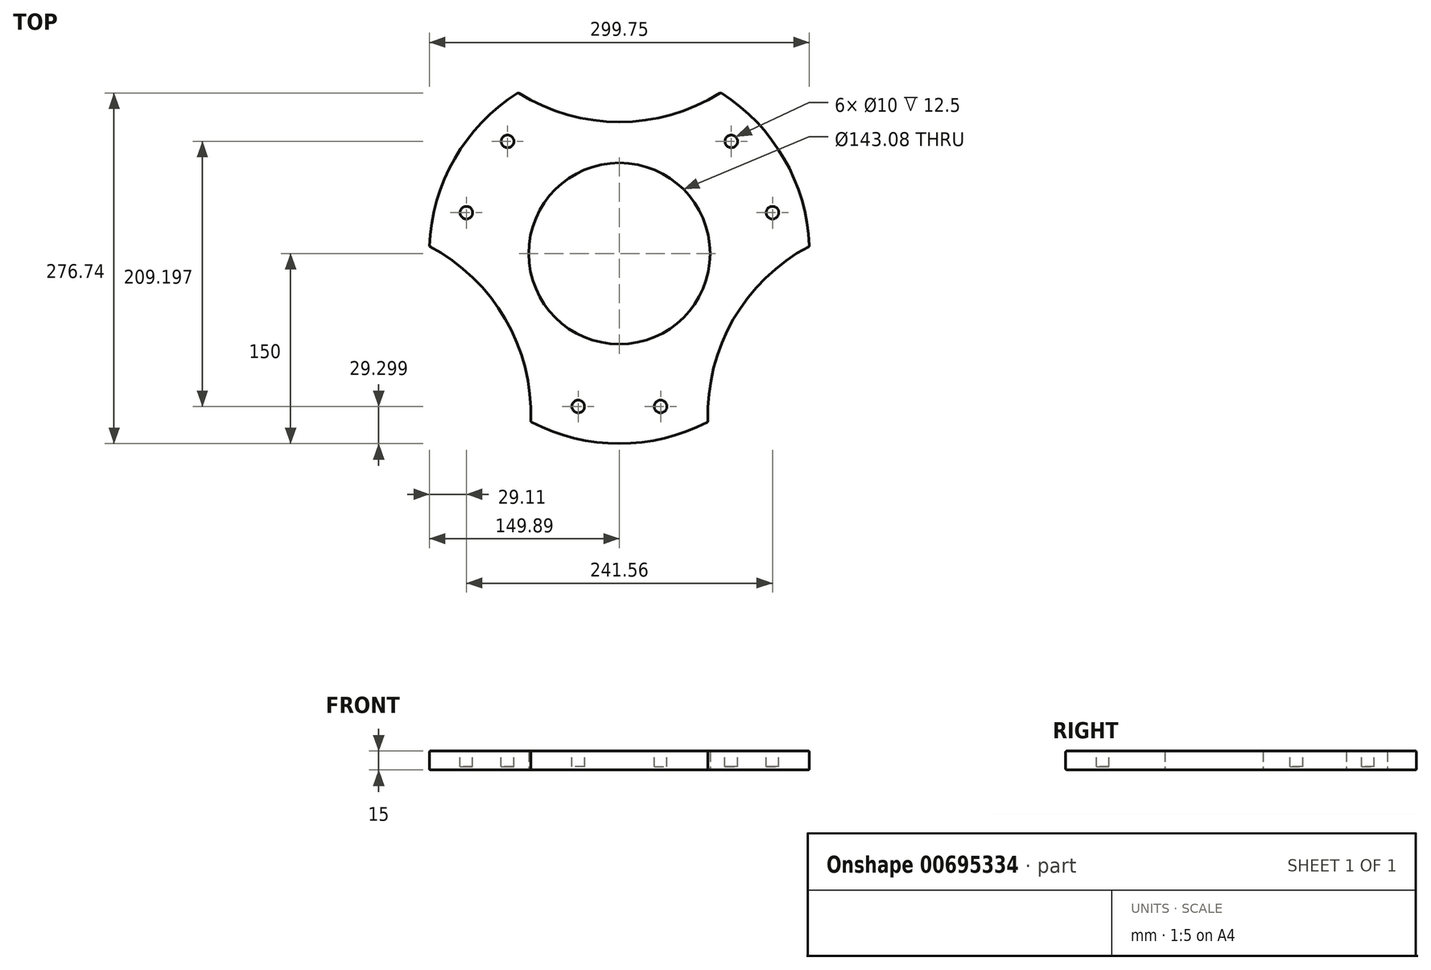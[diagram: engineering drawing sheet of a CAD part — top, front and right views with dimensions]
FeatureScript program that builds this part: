
annotation { "Feature Type Name" : "Feature", "Feature Type Description" : "" }
export const myFeature = defineFeature(function(context is Context, id is Id, definition is map)
    precondition{}
    {
        {
            var Q0;
            Q0=qCreatedBy(makeId("Top.planeOp"),FACE);
            var sketch = newSketch(context, id + "F0", { "sketchPlane" : qUnion([Q0])});
            skLineSegment(sketch, "E0", {"start": v(0, 0) * mm, "end": v(0, -150) * mm, "construction": true});
            skArc(sketch, "E1", {"start": v(-61.95, 35.77) * mm, "mid": v(-61.95, -35.77) * mm, "end": v(0, -71.54) * mm});
            skArc(sketch, "E2", {"start": v(-129.9, 75) * mm, "mid": v(-144.12, 41.6) * mm, "end": v(-149.89, 5.76) * mm});
            skLineSegment(sketch, "E3", {"start": v(0, 0) * mm, "end": v(-129.9, -75) * mm, "construction": true});
            skArc(sketch, "E4", {"start": v(-69.95, -132.69) * mm, "mid": v(-89.94, -51.93) * mm, "end": v(-149.89, 5.76) * mm});
            skLineSegment(sketch, "E5", {"start": v(0, 0) * mm, "end": v(-129.9, 75) * mm, "construction": true});
            skLineSegment(sketch, "E6", {"start": v(-129.9, 75) * mm, "end": v(-61.95, 35.77) * mm});
            skLineSegment(sketch, "E7", {"start": v(0, -71.54) * mm, "end": v(0, -150) * mm});
            skArc(sketch, "E8.trimOffspring", {"start": v(-69.95, -132.69) * mm, "mid": v(-36.03, -145.6) * mm, "end": v(0, -150) * mm});
            skSolve(sketch);
        }
        {
            var Q0;
            Q0=makeQuery(id+"F0.imprint","IMPRINT",FACE,{"disambiguationData":[TD([[makeQuery(id+"F0.imprint","IMPRINT",EDGE,{"derivedFrom":sQuery(id+"F0.wireOp",EDGE,"E1")}),-1.0]])]});
            extrude(context, id + "F1", {"entities" : qUnion([Q0]), "depth" : 15 * mm});
        }
        {
            var Q0;
            Q0=makeQuery(id+"F1.opExtrude","CAP_FACE",FACE,{"disambiguationData":[OSD([sQuery(id+"F0.wireOp",EDGE,"E1"),sQuery(id+"F0.wireOp",EDGE,"E2"),sQuery(id+"F0.wireOp",EDGE,"E4"),sQuery(id+"F0.wireOp",EDGE,"E6"),sQuery(id+"F0.wireOp",EDGE,"E7"),sQuery(id+"F0.wireOp",EDGE,"E8.trimOffspring")])],"isStart":false});
            var sketch = newSketch(context, id + "F2", { "sketchPlane" : qUnion([Q0])});
            skCircle(sketch, "E9", {"center": v(-32.5, -120.7) * mm, "radius": 5 * mm});
            skCircle(sketch, "E10", {"center": v(0, 0) * mm, "radius": 125 * mm, "construction": true});
            skLineSegment(sketch, "E11.0", {"start": v(0, 0) * mm, "end": v(-129.9, -75) * mm, "construction": true});
            skLineSegment(sketch, "E12.0", {"start": v(0, 0) * mm, "end": v(0, -150) * mm, "construction": true});
            skSolve(sketch);
        }
        {
            var Q0;
            Q0=makeQuery(id+"F2.imprint","IMPRINT",FACE,{"disambiguationData":[TD([[makeQuery(id+"F2.imprint","IMPRINT",EDGE,{"derivedFrom":sQuery(id+"F2.wireOp",EDGE,"E9")}),1.0]])]});
            extrude(context, id + "F3", {"entities" : qUnion([Q0]), "oppositeDirection" : true, "depth" : 12.5 * mm});
        }
        {
            var Q0;
            Q0=sQuery(id+"F0.wireOp",EDGE,"E3");
            cPlane(context, id + "F4", {"entities" : qUnion([Q0]), "cplaneType" : CPlaneType.LINE_ANGLE, "offset" : 150 * mm, "angle" : 0 * degree, "width" : 150 * mm, "height" : 150 * mm});
        }
        {
            var Q0;
            Q0=makeQuery(id+"F3.opExtrude","SWEPT_BODY",BODY,{"disambiguationData":[OSD([sQuery(id+"F2.wireOp",EDGE,"E9")])]});
            var Q1;
            Q1=qCreatedBy(id+"F4.planeOp",FACE);
            mirror(context, id + "F5", {"entities" : qUnion([Q0]), "mirrorPlane" : qUnion([Q1])});
        }
        {
            var Q0;
            Q0=makeQuery(id+"F3.opExtrude","SWEPT_BODY",BODY,{"disambiguationData":[OSD([sQuery(id+"F2.wireOp",EDGE,"E9")])]});
            var Q1;
            Q1=makeQuery(id+"F5.opPattern","COPY",BODY,{"derivedFrom":makeQuery(id+"F3.opExtrude","SWEPT_BODY",BODY,{"disambiguationData":[OSD([sQuery(id+"F2.wireOp",EDGE,"E9")])]}),"instanceName":"1"});
            var Q2;
            Q2=makeQuery(id+"F1.opExtrude","SWEPT_BODY",BODY,{"disambiguationData":[OSD([sQuery(id+"F0.wireOp",EDGE,"E1"),sQuery(id+"F0.wireOp",EDGE,"E2"),sQuery(id+"F0.wireOp",EDGE,"E4"),sQuery(id+"F0.wireOp",EDGE,"E6"),sQuery(id+"F0.wireOp",EDGE,"E7"),sQuery(id+"F0.wireOp",EDGE,"E8.trimOffspring")])]});
            booleanBodies(context, id + "F6", {"operationType" : BooleanOperationType.SUBTRACTION, "tools" : qUnion([Q0, Q1]), "targets" : qUnion([Q2])});
        }
        {
            var Q0;
            Q0=makeQuery(id+"F1.opExtrude","SWEPT_BODY",BODY,{"disambiguationData":[OSD([sQuery(id+"F0.wireOp",EDGE,"E1"),sQuery(id+"F0.wireOp",EDGE,"E2"),sQuery(id+"F0.wireOp",EDGE,"E4"),sQuery(id+"F0.wireOp",EDGE,"E6"),sQuery(id+"F0.wireOp",EDGE,"E7"),sQuery(id+"F0.wireOp",EDGE,"E8.trimOffspring")])]});
            var Q1;
            Q1=makeQuery(id+"F1.opExtrude","SWEPT_FACE",FACE,{"disambiguationData":[OSD([sQuery(id+"F0.wireOp",EDGE,"E1")])]});
            circularPattern(context, id + "F7", {"entities" : qUnion([Q0]), "axis" : qUnion([Q1]), "angle" : 360 * degree, "instanceCount" : 3, "equalSpace" : true, "computeTransformsWithoutBuiltin" : true});
        }
        {
            var Q0;
            Q0=makeQuery(id+"F1.opExtrude","SWEPT_BODY",BODY,{"disambiguationData":[OSD([sQuery(id+"F0.wireOp",EDGE,"E1"),sQuery(id+"F0.wireOp",EDGE,"E2"),sQuery(id+"F0.wireOp",EDGE,"E4"),sQuery(id+"F0.wireOp",EDGE,"E6"),sQuery(id+"F0.wireOp",EDGE,"E7"),sQuery(id+"F0.wireOp",EDGE,"E8.trimOffspring")])]});
            var Q1;
            Q1=makeQuery(id+"F7.opPattern","COPY",BODY,{"derivedFrom":makeQuery(id+"F1.opExtrude","SWEPT_BODY",BODY,{"disambiguationData":[OSD([sQuery(id+"F0.wireOp",EDGE,"E1"),sQuery(id+"F0.wireOp",EDGE,"E2"),sQuery(id+"F0.wireOp",EDGE,"E4"),sQuery(id+"F0.wireOp",EDGE,"E6"),sQuery(id+"F0.wireOp",EDGE,"E7"),sQuery(id+"F0.wireOp",EDGE,"E8.trimOffspring")])]}),"instanceName":"2"});
            var Q2;
            Q2=makeQuery(id+"F7.opPattern","COPY",BODY,{"derivedFrom":makeQuery(id+"F1.opExtrude","SWEPT_BODY",BODY,{"disambiguationData":[OSD([sQuery(id+"F0.wireOp",EDGE,"E1"),sQuery(id+"F0.wireOp",EDGE,"E2"),sQuery(id+"F0.wireOp",EDGE,"E4"),sQuery(id+"F0.wireOp",EDGE,"E6"),sQuery(id+"F0.wireOp",EDGE,"E7"),sQuery(id+"F0.wireOp",EDGE,"E8.trimOffspring")])]}),"instanceName":"1"});
            booleanBodies(context, id + "F8", {"operationType" : BooleanOperationType.UNION, "tools" : qUnion([Q0, Q1, Q2])});
        }
        {
            var Q0;
            Q0=makeQuery(id+"F8.opBoolean","MERGE",EDGE,{"derivedFrom":[makeQuery(id+"F1.opExtrude","CAP_EDGE",EDGE,{"disambiguationData":[OSD([sQuery(id+"F0.wireOp",EDGE,"E8.trimOffspring")])],"isStart":false}),makeQuery(id+"F7.opPattern","COPY",EDGE,{"derivedFrom":makeQuery(id+"F1.opExtrude","CAP_EDGE",EDGE,{"disambiguationData":[OSD([sQuery(id+"F0.wireOp",EDGE,"E2")])],"isStart":false}),"instanceName":"1"})]});
            var Q1;
            Q1=makeQuery(id+"F7.opPattern","COPY",EDGE,{"derivedFrom":makeQuery(id+"F1.opExtrude","SWEPT_EDGE",EDGE,{"disambiguationData":[OSD([sQuery(id+"F0.wireOp",EDGE,"E2"),sQuery(id+"F0.wireOp",EDGE,"E4")])]}),"instanceName":"1"});
            var Q2;
            Q2=makeQuery(id+"F7.opPattern","COPY",EDGE,{"derivedFrom":makeQuery(id+"F1.opExtrude","CAP_EDGE",EDGE,{"disambiguationData":[OSD([sQuery(id+"F0.wireOp",EDGE,"E4")])],"isStart":false}),"instanceName":"1"});
            var Q3;
            Q3=makeQuery(id+"F7.opPattern","COPY",EDGE,{"derivedFrom":makeQuery(id+"F1.opExtrude","SWEPT_EDGE",EDGE,{"disambiguationData":[OSD([sQuery(id+"F0.wireOp",EDGE,"E4"),sQuery(id+"F0.wireOp",EDGE,"E8.trimOffspring")])]}),"instanceName":"1"});
            var Q4;
            Q4=makeQuery(id+"F8.opBoolean","MERGE",EDGE,{"derivedFrom":[makeQuery(id+"F7.opPattern","COPY",EDGE,{"derivedFrom":makeQuery(id+"F1.opExtrude","CAP_EDGE",EDGE,{"disambiguationData":[OSD([sQuery(id+"F0.wireOp",EDGE,"E8.trimOffspring")])],"isStart":false}),"instanceName":"1"}),makeQuery(id+"F7.opPattern","COPY",EDGE,{"derivedFrom":makeQuery(id+"F1.opExtrude","CAP_EDGE",EDGE,{"disambiguationData":[OSD([sQuery(id+"F0.wireOp",EDGE,"E2")])],"isStart":false}),"instanceName":"2"})]});
            var Q5;
            Q5=makeQuery(id+"F7.opPattern","COPY",EDGE,{"derivedFrom":makeQuery(id+"F1.opExtrude","SWEPT_EDGE",EDGE,{"disambiguationData":[OSD([sQuery(id+"F0.wireOp",EDGE,"E2"),sQuery(id+"F0.wireOp",EDGE,"E4")])]}),"instanceName":"2"});
            var Q6;
            Q6=makeQuery(id+"F7.opPattern","COPY",EDGE,{"derivedFrom":makeQuery(id+"F1.opExtrude","CAP_EDGE",EDGE,{"disambiguationData":[OSD([sQuery(id+"F0.wireOp",EDGE,"E4")])],"isStart":false}),"instanceName":"2"});
            var Q7;
            Q7=makeQuery(id+"F7.opPattern","COPY",EDGE,{"derivedFrom":makeQuery(id+"F1.opExtrude","SWEPT_EDGE",EDGE,{"disambiguationData":[OSD([sQuery(id+"F0.wireOp",EDGE,"E4"),sQuery(id+"F0.wireOp",EDGE,"E8.trimOffspring")])]}),"instanceName":"2"});
            var Q8;
            Q8=makeQuery(id+"F8.opBoolean","MERGE",EDGE,{"derivedFrom":[makeQuery(id+"F1.opExtrude","CAP_EDGE",EDGE,{"disambiguationData":[OSD([sQuery(id+"F0.wireOp",EDGE,"E2")])],"isStart":false}),makeQuery(id+"F7.opPattern","COPY",EDGE,{"derivedFrom":makeQuery(id+"F1.opExtrude","CAP_EDGE",EDGE,{"disambiguationData":[OSD([sQuery(id+"F0.wireOp",EDGE,"E8.trimOffspring")])],"isStart":false}),"instanceName":"2"})]});
            var Q9;
            Q9=makeQuery(id+"F1.opExtrude","CAP_EDGE",EDGE,{"disambiguationData":[OSD([sQuery(id+"F0.wireOp",EDGE,"E4")])],"isStart":false});
            var Q10;
            Q10=makeQuery(id+"F1.opExtrude","SWEPT_EDGE",EDGE,{"disambiguationData":[OSD([sQuery(id+"F0.wireOp",EDGE,"E4"),sQuery(id+"F0.wireOp",EDGE,"E8.trimOffspring")])]});
            var Q11;
            Q11=makeQuery(id+"F8.opBoolean","MERGE",EDGE,{"derivedFrom":[makeQuery(id+"F1.opExtrude","CAP_EDGE",EDGE,{"disambiguationData":[OSD([sQuery(id+"F0.wireOp",EDGE,"E8.trimOffspring")])],"isStart":true}),makeQuery(id+"F7.opPattern","COPY",EDGE,{"derivedFrom":makeQuery(id+"F1.opExtrude","CAP_EDGE",EDGE,{"disambiguationData":[OSD([sQuery(id+"F0.wireOp",EDGE,"E2")])],"isStart":true}),"instanceName":"1"})]});
            var Q12;
            Q12=makeQuery(id+"F1.opExtrude","CAP_EDGE",EDGE,{"disambiguationData":[OSD([sQuery(id+"F0.wireOp",EDGE,"E4")])],"isStart":true});
            var Q13;
            Q13=makeQuery(id+"F7.opPattern","COPY",EDGE,{"derivedFrom":makeQuery(id+"F1.opExtrude","CAP_EDGE",EDGE,{"disambiguationData":[OSD([sQuery(id+"F0.wireOp",EDGE,"E4")])],"isStart":true}),"instanceName":"1"});
            var Q14;
            Q14=makeQuery(id+"F8.opBoolean","MERGE",EDGE,{"derivedFrom":[makeQuery(id+"F7.opPattern","COPY",EDGE,{"derivedFrom":makeQuery(id+"F1.opExtrude","CAP_EDGE",EDGE,{"disambiguationData":[OSD([sQuery(id+"F0.wireOp",EDGE,"E8.trimOffspring")])],"isStart":true}),"instanceName":"1"}),makeQuery(id+"F7.opPattern","COPY",EDGE,{"derivedFrom":makeQuery(id+"F1.opExtrude","CAP_EDGE",EDGE,{"disambiguationData":[OSD([sQuery(id+"F0.wireOp",EDGE,"E2")])],"isStart":true}),"instanceName":"2"})]});
            var Q15;
            Q15=makeQuery(id+"F7.opPattern","COPY",EDGE,{"derivedFrom":makeQuery(id+"F1.opExtrude","CAP_EDGE",EDGE,{"disambiguationData":[OSD([sQuery(id+"F0.wireOp",EDGE,"E4")])],"isStart":true}),"instanceName":"2"});
            var Q16;
            Q16=makeQuery(id+"F8.opBoolean","MERGE",EDGE,{"derivedFrom":[makeQuery(id+"F1.opExtrude","CAP_EDGE",EDGE,{"disambiguationData":[OSD([sQuery(id+"F0.wireOp",EDGE,"E2")])],"isStart":true}),makeQuery(id+"F7.opPattern","COPY",EDGE,{"derivedFrom":makeQuery(id+"F1.opExtrude","CAP_EDGE",EDGE,{"disambiguationData":[OSD([sQuery(id+"F0.wireOp",EDGE,"E8.trimOffspring")])],"isStart":true}),"instanceName":"2"})]});
            var Q17;
            {var subQ0=makeQuery(id+"F1.opExtrude","CAP_EDGE",EDGE,{"disambiguationData":[OSD([sQuery(id+"F0.wireOp",EDGE,"E1")])],"isStart":true});Q17=makeQuery(id+"F8.opBoolean","MERGE",EDGE,{"derivedFrom":[subQ0,makeQuery(id+"F7.opPattern","COPY",EDGE,{"derivedFrom":subQ0,"instanceName":"1"}),makeQuery(id+"F7.opPattern","COPY",EDGE,{"derivedFrom":subQ0,"instanceName":"2"})]});}
            var Q18;
            {var subQ0=makeQuery(id+"F1.opExtrude","CAP_EDGE",EDGE,{"disambiguationData":[OSD([sQuery(id+"F0.wireOp",EDGE,"E1")])],"isStart":false});Q18=makeQuery(id+"F8.opBoolean","MERGE",EDGE,{"derivedFrom":[subQ0,makeQuery(id+"F7.opPattern","COPY",EDGE,{"derivedFrom":subQ0,"instanceName":"1"}),makeQuery(id+"F7.opPattern","COPY",EDGE,{"derivedFrom":subQ0,"instanceName":"2"})]});}
            fillet(context, id + "F9", {"entities" : qUnion([Q0, Q1, Q2, Q3, Q4, Q5, Q6, Q7, Q8, Q9, Q10, Q11, Q12, Q13, Q14, Q15, Q16, Q17, Q18]), "radius" : 1 * mm, "tangentPropagation" : true, "allowEdgeOverflow" : false});
        }
    });
